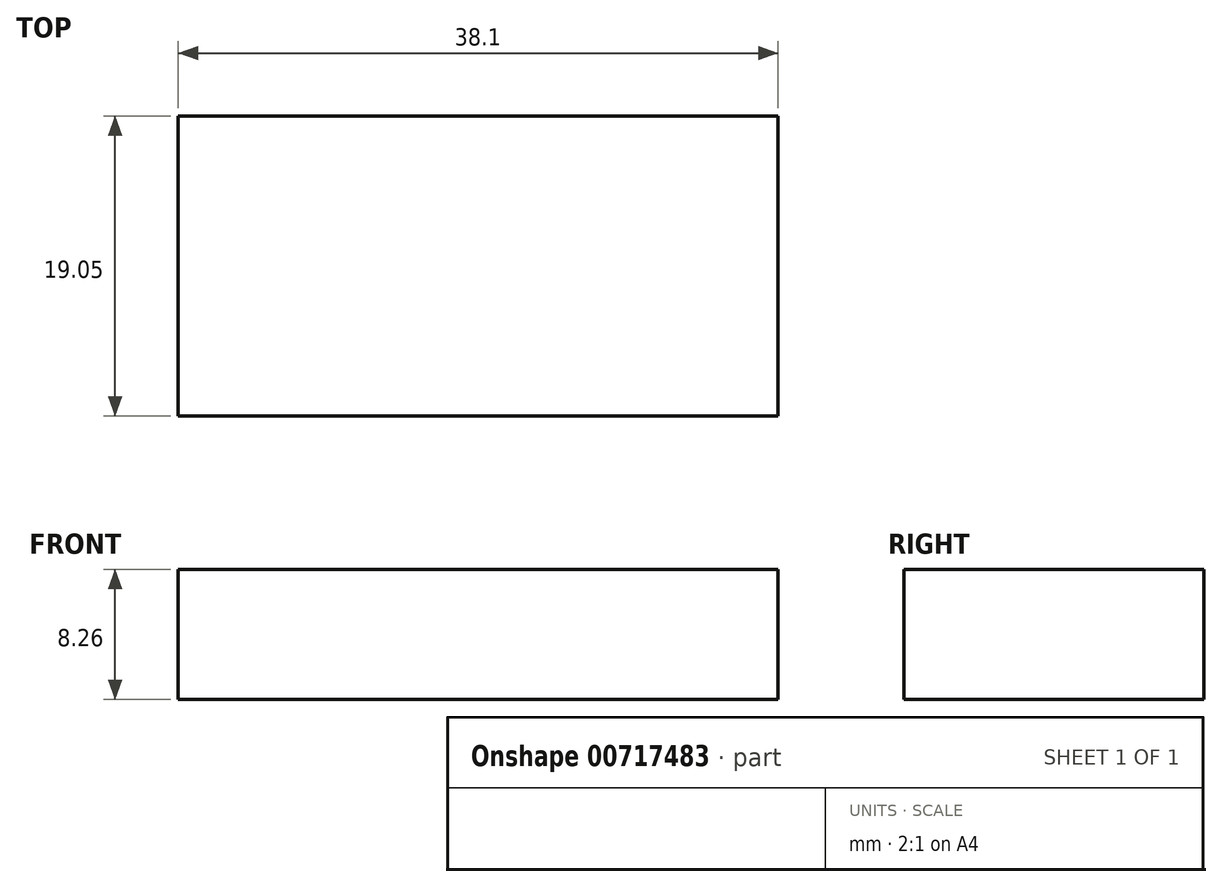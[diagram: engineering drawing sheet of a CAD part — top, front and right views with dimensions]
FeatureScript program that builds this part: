
annotation { "Feature Type Name" : "Feature", "Feature Type Description" : "" }
export const myFeature = defineFeature(function(context is Context, id is Id, definition is map)
    precondition{}
    {
        {
            var Q0;
            Q0=qCreatedBy(makeId("Top.planeOp"),FACE);
            var sketch = newSketch(context, id + "F0", { "sketchPlane" : qUnion([Q0])});
            skLineSegment(sketch, "E0.bottom", {"start": v(-38.1, 19.05) * mm, "end": v(0, 19.05) * mm});
            skLineSegment(sketch, "E0.top", {"start": v(-38.1, 0) * mm, "end": v(0, 0) * mm});
            skLineSegment(sketch, "E0.left", {"start": v(-38.1, 19.05) * mm, "end": v(-38.1, 0) * mm});
            skLineSegment(sketch, "E0.right", {"start": v(0, 19.05) * mm, "end": v(0, 0) * mm});
            skSolve(sketch);
        }
        {
            var Q0;
            Q0 = qSketchRegion(id + "F0", true);
            extrude(context, id + "F1", {"entities" : qUnion([Q0]), "depth" : 8.25 * mm, "offsetDistance" : 25.4 * mm});
        }
    });
